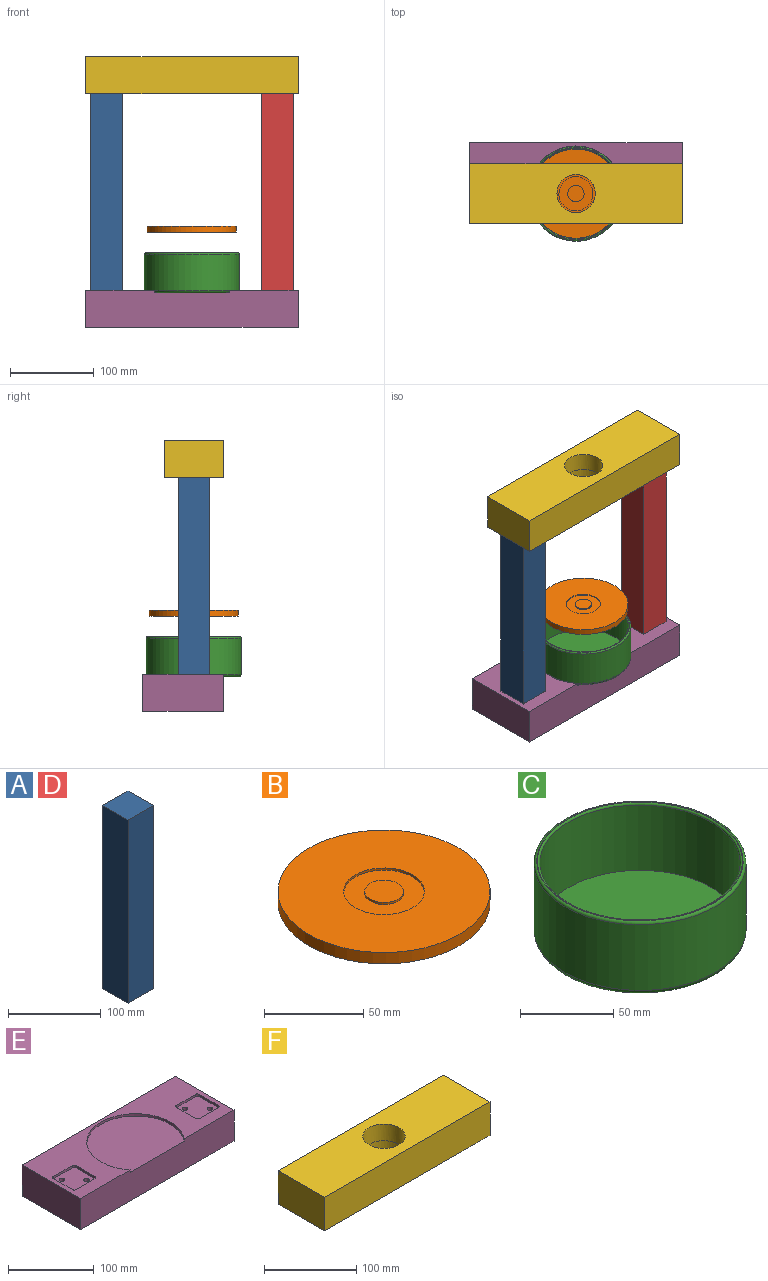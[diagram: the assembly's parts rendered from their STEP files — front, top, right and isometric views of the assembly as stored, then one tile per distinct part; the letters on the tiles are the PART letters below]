
ASSEMBLY  parts=6 mates=5
PART A: 6 faces, bbox 38.1x38.1x241.3 mm
  f0: plane 241.3x38.1mm, normal (0,1,0), area 9193.5mm2, adj f1,f3,f4,f5
  f1: plane 241.3x38.1mm, normal (-1,0,0), area 9193.5mm2, adj f0,f2,f4,f5
  f2: plane 241.3x38.1mm, normal (0,-1,0), area 9193.5mm2, adj f1,f3,f4,f5
  f3: plane 241.3x38.1mm, normal (1,0,0), area 9193.5mm2, adj f0,f2,f4,f5
  f4: plane 38.1x38.1mm, normal (0,0,1), area 1451.6mm2, adj f0,f1,f2,f3
  f5: plane 38.1x38.1mm, normal (0,0,-1), area 1451.6mm2, adj f0,f1,f2,f3
PART B: 7 faces, bbox 106.7x106.7x7 mm
  f0: cylinder r=53.34mm len=106.68mm, axis (0,0,-1), area 2341mm2, adj f1,f2
  f1: plane 106.68x106.68mm, normal (0,0,1), area 7641.1mm2, adj f0,f3
  f2: plane 106.68x106.68mm, normal (0,0,-1), area 8938.3mm2, adj f0
  f3: cylinder r=20.32mm len=40.64mm, axis (0,0,1), area 162.1mm2, adj f1,f4
  f4: plane 40.64x40.64mm, normal (0,0,1), area 996.7mm2, adj f3,f5
  f5: cylinder r=9.78mm len=19.56mm, axis (0,0,-1), area 78mm2, adj f4,f6
  f6: plane 19.56x19.56mm, normal (0,0,1), area 300.4mm2, adj f5
PART C: 8 faces, bbox 122.9x122.9x47.8 mm
  f0: plane 110.49x110.49mm, normal (0,0,1), area 131.8mm2, adj f1,f7
  f1: torus R=55.25mm, axis (0,0,-1), area 845.5mm2, adj f0,f2
  f2: cylinder r=56.77mm len=113.54mm, axis (0,0,-1), area 15356.6mm2, adj f1,f3
  f3: torus R=53.59mm, axis (0,0,-1), area 1742.8mm2, adj f2,f4
  f4: plane 107.19x107.19mm, normal (0,0,-1), area 9023.6mm2, adj f3
  f5: plane 107.44x107.44mm, normal (0,0,1), area 9066.5mm2, adj f6
  f6: cylinder r=53.72mm len=107.44mm, axis (0,0,-1), area 14446.3mm2, adj f5,f7
  f7: torus R=54.86mm, axis (0,0,-1), area 610.7mm2, adj f0,f6
PART D: same geometry as A
PART E: 30 faces, bbox 254x96.5x44.5 mm
  f0: plane 254x96.52mm, normal (0,0,1), area 12792.2mm2, adj f1,f2,f3,f4,f6,f7,f8,f9
  f1: plane 254x44.45mm, normal (0,1,0), area 11290.3mm2, adj f0,f2,f4,f5
  f2: plane 96.52x44.45mm, normal (-1,0,0), area 4290.3mm2, adj f0,f1,f3,f5
  f3: plane 254x44.45mm, normal (0,-1,0), area 10994.8mm2, adj f0,f2,f4,f5,f24,f25
  f4: plane 96.52x44.45mm, normal (1,0,0), area 4290.3mm2, adj f0,f1,f3,f5
  f5: plane 254x96.52mm, normal (0,0,-1), area 24389.4mm2, adj f1,f2,f3,f4,f26,f27,f28,f29
  f6: plane 31.28x3.3mm, normal (1,0,0), area 103.3mm2, adj f0,f7,f13,f14
  f7: cylinder r=3.17mm len=3.3mm, axis (0,0,1), area 14.8mm2, adj f0,f6,f8,f14
  f8: plane 31.75x3.3mm, normal (0,1,0), area 104.8mm2, adj f0,f7,f9,f14
  f9: cylinder r=3.17mm len=3.3mm, axis (0,0,1), area 16.5mm2, adj f0,f8,f10,f14
  f10: plane 31.24x3.3mm, normal (-1,0,0), area 103.2mm2, adj f0,f9,f11,f14
  f11: cylinder r=3.17mm len=3.3mm, axis (0,0,1), area 16.5mm2, adj f0,f10,f12,f14
  f12: plane 31.24x3.3mm, normal (0,-1,0), area 103.2mm2, adj f0,f11,f13,f14
  f13: cylinder r=3.17mm len=3.3mm, axis (0,0,1), area 16.5mm2, adj f0,f6,f12,f14
  f14: plane 37.59x37.59mm, normal (0,0,1), area 1341.3mm2, adj f6,f7,f8,f9,f10,f11,f12,f13
  f15: plane 31.24x3.3mm, normal (-1,0,0), area 103.2mm2, adj f0,f16,f22,f23
  f16: cylinder r=3.17mm len=3.3mm, axis (0,0,1), area 16.5mm2, adj f0,f15,f17,f23
  f17: plane 31.24x3.3mm, normal (0,-1,0), area 103.2mm2, adj f0,f16,f18,f23
  f18: cylinder r=3.17mm len=3.3mm, axis (0,0,1), area 16.5mm2, adj f0,f17,f19,f23
  f19: plane 31.24x3.3mm, normal (1,0,0), area 103.2mm2, adj f0,f18,f20,f23
  f20: cylinder r=3.17mm len=3.3mm, axis (0,0,1), area 16.5mm2, adj f0,f19,f21,f23
  f21: plane 31.24x3.3mm, normal (0,1,0), area 103.2mm2, adj f0,f20,f22,f23
  f22: cylinder r=3.17mm len=3.3mm, axis (0,0,1), area 16.5mm2, adj f0,f15,f21,f23
  f23: plane 37.59x37.59mm, normal (0,0,1), area 1341.2mm2, adj f15,f16,f17,f18,f19,f20,f21,f22
  f24: plane 114.3x92.71mm, normal (0,0,1), area 8914.8mm2, adj f3,f25
  f25: cylinder r=57.15mm len=114.3mm, axis (0,0,1), area 846.3mm2, adj f0,f3,f24
  f26: cylinder r=3.17mm len=41.15mm, axis (0,0,1), area 820.9mm2, adj f5,f14
  f27: cylinder r=3.17mm len=41.15mm, axis (0,0,1), area 820.9mm2, adj f5,f23
  f28: cylinder r=3.17mm len=41.15mm, axis (0,0,1), area 820.9mm2, adj f5,f23
  f29: cylinder r=3.17mm len=41.15mm, axis (0,0,1), area 820.9mm2, adj f5,f14
PART F: 27 faces, bbox 254x71.1x44.5 mm
  f0: cylinder r=22.86mm len=45.72mm, axis (0,0,-1), area 3174mm2, adj f6,f25
  f1: plane 254x71.12mm, normal (0,0,-1), area 13049.1mm2, adj f2,f3,f4,f5,f7,f8,f9,f10
  f2: plane 254x44.45mm, normal (0,1,0), area 11290.3mm2, adj f1,f3,f5,f6
  f3: plane 71.12x44.45mm, normal (-1,0,0), area 3161.3mm2, adj f1,f2,f4,f6
  f4: plane 254x44.45mm, normal (0,-1,0), area 11290.3mm2, adj f1,f3,f5,f6
  f5: plane 71.12x44.45mm, normal (1,0,0), area 3161.3mm2, adj f1,f2,f4,f6
  f6: plane 254x71.12mm, normal (0,0,1), area 16422.7mm2, adj f0,f2,f3,f4,f5
  f7: plane 31.75x3.3mm, normal (1,0,0), area 104.8mm2, adj f1,f8,f14,f15
  f8: cylinder r=3.17mm len=3.3mm, axis (0,0,-1), area 16.5mm2, adj f1,f7,f9,f15
  f9: plane 31.75x3.3mm, normal (0,-1,0), area 104.8mm2, adj f1,f8,f10,f15
  f10: cylinder r=3.17mm len=3.3mm, axis (0,0,-1), area 16.5mm2, adj f1,f9,f11,f15
  f11: plane 31.75x3.3mm, normal (-1,0,0), area 104.8mm2, adj f1,f10,f12,f15
  f12: cylinder r=3.17mm len=3.3mm, axis (0,0,-1), area 16.5mm2, adj f1,f11,f13,f15
  f13: plane 31.75x3.3mm, normal (0,1,0), area 104.8mm2, adj f1,f12,f14,f15
  f14: cylinder r=3.17mm len=3.3mm, axis (0,0,-1), area 16.5mm2, adj f1,f7,f13,f15
  f15: plane 38.1x38.1mm, normal (0,0,-1), area 1443mm2, adj f7,f8,f9,f10,f11,f12,f13,f14
  f16: plane 31.75x3.3mm, normal (-1,0,0), area 104.8mm2, adj f1,f17,f23,f24
  f17: cylinder r=3.17mm len=3.3mm, axis (0,0,-1), area 16.5mm2, adj f1,f16,f18,f24
  f18: plane 31.75x3.3mm, normal (0,1,0), area 104.8mm2, adj f1,f17,f19,f24
  f19: cylinder r=3.17mm len=3.3mm, axis (0,0,-1), area 16.5mm2, adj f1,f18,f20,f24
  f20: plane 31.75x3.3mm, normal (1,0,0), area 104.8mm2, adj f1,f19,f21,f24
  f21: cylinder r=3.17mm len=3.3mm, axis (0,0,-1), area 16.5mm2, adj f1,f20,f22,f24
  f22: plane 31.75x3.3mm, normal (0,-1,0), area 104.8mm2, adj f1,f21,f23,f24
  f23: cylinder r=3.17mm len=3.3mm, axis (0,0,-1), area 16.5mm2, adj f1,f16,f22,f24
  f24: plane 38.1x38.1mm, normal (0,0,-1), area 1443mm2, adj f16,f17,f18,f19,f20,f21,f22,f23
  f25: plane 52.07x52.07mm, normal (0,0,-1), area 487.7mm2, adj f0,f26
  f26: cylinder r=26.04mm len=52.07mm, axis (0,0,-1), area 3656.4mm2, adj f1,f25
PLACE A t=(-103.71,2.36,102.37)mm
PLACE B rot(axis=(0,0,-1),47.6deg) t=(-1.86,2.62,175.08)mm
PLACE C rot(axis=(0,0,1),11deg) t=(-1.86,2.62,102.6)mm
PLACE D t=(99.99,2.36,102.37)mm
PLACE E t=(-1.86,15.32,61.22)mm fixed
PLACE F t=(-1.61,2.36,340.37)mm
MATE fastened E.f14 <-> D.f5  axis (0,0,1) through (99.99,2.36,102.37)mm
MATE fastened A.f5 <-> E.f23  axis (0,0,-1) through (-103.71,2.36,102.37)mm
MATE fastened F.f15 <-> D.f4  axis (0,0,-1) through (99.99,2.36,343.67)mm
MATE cylindrical C.f1 <-> E.f25  axis (0,0,-1) through (-1.86,2.62,127.31)mm
MATE cylindrical B.f0 <-> C.f1  axis (0,0,1) through (-1.86,2.62,182.06)mm
